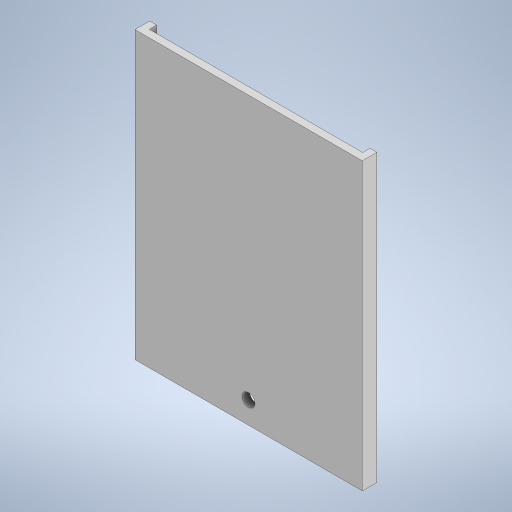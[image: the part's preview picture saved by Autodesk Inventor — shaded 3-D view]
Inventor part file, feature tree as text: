
AUTODESK INVENTOR PART (.ipt)
format: ipt  version: 2023.1 (Build 271208000, 208)  size: 220,160 bytes
history: native  units: mm
features: extrude x3, sketch x2, other x1
ambient origin geometry x8: Origin, YZ Plane, XZ Plane, XY Plane, X Axis, Y Axis, Z Axis, Center Point
bodies: Body1 (feature_tree)
feature tree (6):
  other  "솔리드1"
  sketch  "스케치1"
  extrude  "돌출1"  Depth=62.0mm
  extrude  "돌출2"  Depth=78.0mm
  sketch  "스케치2"
  extrude  "돌출4"  Depth=1.9mm
